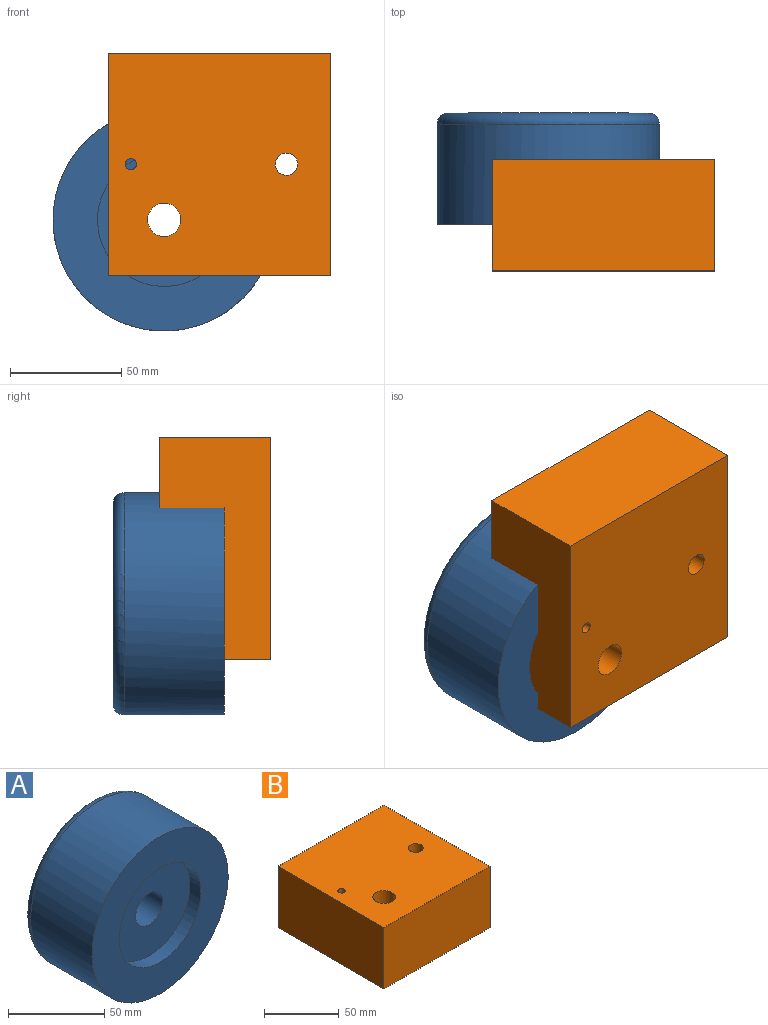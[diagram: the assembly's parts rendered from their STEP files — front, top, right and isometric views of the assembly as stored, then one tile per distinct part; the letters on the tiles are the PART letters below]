
ASSEMBLY  parts=2 mates=1
PART A: 7 faces, bbox 108.2x50x108.2 mm
  f0: cylinder r=50mm len=100mm, axis (0,1,0), area 14137.2mm2, adj f5,f6
  f1: plane 90x90mm, normal (0,1,0), area 6047.6mm2, adj f2,f6
  f2: cylinder r=10mm len=42mm, axis (0,1,0), area 2638.9mm2, adj f1,f3
  f3: plane 60x60mm, normal (0,-1,0), area 2513.3mm2, adj f2,f4
  f4: cylinder r=30mm len=60mm, axis (0,1,0), area 1508mm2, adj f3,f5
  f5: plane 100x100mm, normal (0,-1,0), area 5026.5mm2, adj f0,f4
  f6: torus R=45mm, axis (0,-1,0), area 2377.7mm2, adj f0,f1
PART B: 9 faces, bbox 100x100x50 mm
  f0: plane 100x50mm, normal (0,-1,0), area 5000mm2, adj f1,f6,f7,f8
  f1: plane 100x50mm, normal (1,0,0), area 5000mm2, adj f0,f2,f7,f8
  f2: plane 100x50mm, normal (0,1,0), area 5000mm2, adj f1,f6,f7,f8
  f3: cylinder r=2.5mm len=50mm, axis (0,0,-1), area 785.4mm2, adj f7,f8
  f4: cylinder r=5mm len=50mm, axis (0,0,-1), area 1570.8mm2, adj f7,f8
  f5: cylinder r=7.5mm len=50mm, axis (0,0,-1), area 2356.2mm2, adj f7,f8
  f6: plane 100x50mm, normal (-1,0,0), area 5000mm2, adj f0,f2,f7,f8
  f7: plane 100x100mm, normal (0,0,1), area 9725.1mm2, adj f0,f1,f2,f3,f4,f5,f6
  f8: plane 100x100mm, normal (0,0,-1), area 9725.1mm2, adj f0,f1,f2,f3,f4,f5,f6
PLACE A t=(144.27,1.31,21.98)mm
PLACE B rot(axis=(1,0,0),90deg) t=(169.27,37.31,46.98)mm
MATE fastened B.f5 <-> A.f0  axis (0,1,0) through (144.27,37.31,21.98)mm
